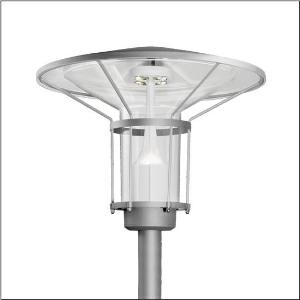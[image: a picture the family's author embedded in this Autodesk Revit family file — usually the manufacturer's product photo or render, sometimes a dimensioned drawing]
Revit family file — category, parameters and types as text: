
# Revit family: laterne_classic_iq___p1_0a_5xa5245ff14h_a382
name_source: partatom
category: Lighting Fixtures
units: mm (PartAtom-declared; Revit-internal decimal feet)

## family parameters
Cut with Voids When Loaded = No
Host = Face
Light Source = No
Part Type = Normal
Room Calculation Point = No
Round Connector Dimension = Use Diameter
Shared = No

## types (1)
- --- (1 x LED, 1360 lm, 10.5 W, 3000K)
    Apparent Load = 11 VA
    CIE Flux Codes = 30 61 91 96 100
    Color Rendering = 70
    Color Temperature = 3000K
    Default Elevation = 1800 mm
    Description = Lantern Classic iQ, mast luminaire, Module 540 iQ-SR, primary light control with 3 zone facetted reflector, of plastic, silver coated, highly specular, structured, primary optical cover: cover, of PMMA, transparent, light distribution: P1.0a, light emission: direct distribution, primary light characteristic: strongly asymmetric, installation type: post-top, LED, High Power LED, rated luminous flux: 1.360lm, luminous efficacy: 130lm/W, light colour: 730, colour temperature: 3000K, control gear: ECG iQ, control: Auto-Match, Temp-Guard, Lumen-Switch, Night-Set, Smart-Wire, Light-Fading, Desk-Remote (wireless, voltage-free reading and setting of iQ features in the workshop via application-optimized NFC function/RFID function), optimised constant luminous flux control (CLO 2.0), Street-Remote, pre-setting: logarithmic dimming characteristic, with terminal, 6-pole, max. 2.5mm², mains connection: 230..240V, AC, 50/60Hz, start of lifetime: 11W, end of service life: 11W, reduction: 5W, luminaire housing, upper part, of glass-fibre reinforced polyester, coated, Siteco® metallic grey (DB 702S), diameter: 750mm, height: 596mm, spigot size: d x l = 76 x 70mm (post-top) | with reducer (optional accessory) 60 x 70mm, post-top mast mounting element, of diecast aluminium, coated, Siteco® metallic grey (DB 702S), Module 540 iQ-SR, traffic white (RAL 9016), equipment: standard, protection rating (complete): IP65, insulation class (complete): insulation class II (safety insulation), certification: CE, ENEC, VDE, packaging unit: 1 piece

Light Distribution: P1.0a
    Height = 596 mm
    Lamp = 1 x LED
    Lamp Light Flux = 1360 lm
    Lamp Power = 10.5 W
    Lamp count = 1
    Length = 750 mm
    Luminous efficacy = 130 lm/W
    Manufacturer = Siteco
    ModVariant = No
    Model = 5XA5245FF14H
    Number of Poles = 1
    OnlyDefault = Yes
    Power Factor = 1
    Product Name = Laterne Classic iQ | P1.0a
    Product group = mast luminaire | pylon top
    ProductGroupID = 6100
    Protection Class = Protection class II
    Protection Degree = IP 65
    RLX_Detail_Level = 1
    RLX_Emergency_Light_Flux = 0 lm
    RLX_Emergency_Type = 0
    RLX_Emergency_Type_DB = No
    RlxData = <blob elided: 93561 chars, md5=5ba98e39>
    Socket = socket
    Standby Power = 0 W
    System Light Flux = 1360 lm
    System Power = 11 W
    Type Comments = factory setting: luminous flux: 100 % | dim-lin: 254 | 419 mA
    Type Image = l_1006052.jpg
    URL = http://relux.com
    VarID = @adj_130603
    Voltage = 0 V
    Weight = 0.00 kg
    Width = 0 mm  [stored 0 ft]

note: [stored X ft] marks values corroborated as IEEE doubles in the binary element streams (Revit-internal decimal feet)

## geometry (parser evidence)
native form markers: Blend x4, Sweep x10
no freeform markers — native parametric forms only
